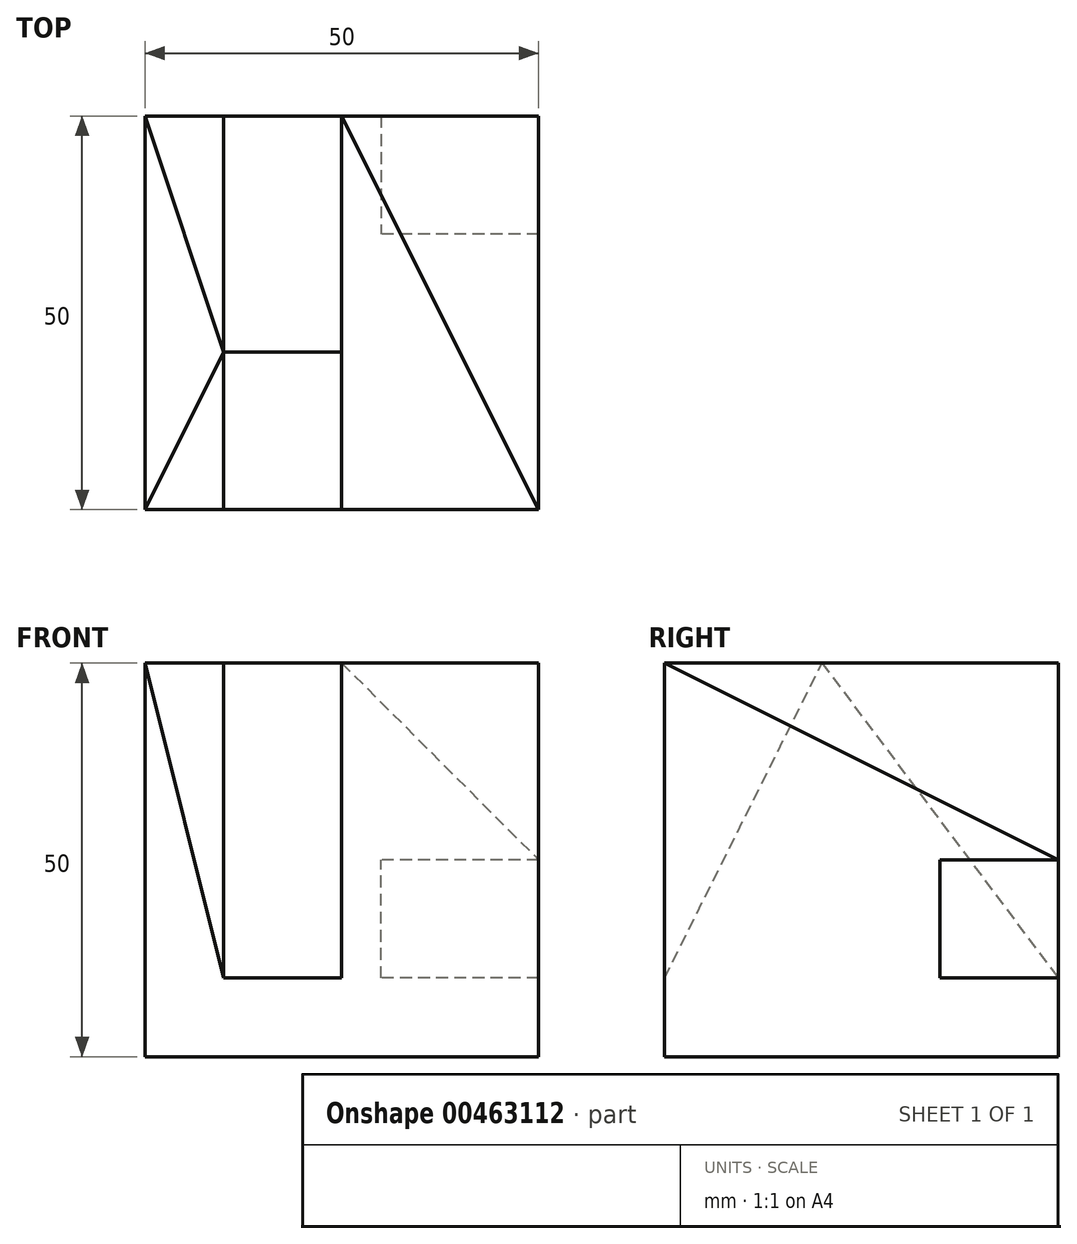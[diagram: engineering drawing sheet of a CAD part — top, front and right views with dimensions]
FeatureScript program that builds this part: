
annotation { "Feature Type Name" : "Feature", "Feature Type Description" : "" }
export const myFeature = defineFeature(function(context is Context, id is Id, definition is map)
    precondition{}
    {
        {
            var Q0;
            Q0=qCreatedBy(makeId("Top.planeOp"),FACE);
            var sketch = newSketch(context, id + "F0", { "sketchPlane" : qUnion([Q0])});
            skLineSegment(sketch, "E0.bottom", {"start": v(0, 0) * mm, "end": v(50, 0) * mm});
            skLineSegment(sketch, "E0.top", {"start": v(0, 50) * mm, "end": v(50, 50) * mm});
            skLineSegment(sketch, "E0.left", {"start": v(0, 0) * mm, "end": v(0, 50) * mm});
            skLineSegment(sketch, "E0.right", {"start": v(50, 0) * mm, "end": v(50, 50) * mm});
            skSolve(sketch);
        }
        {
            var Q0;
            Q0 = qSketchRegion(id + "F0", true);
            extrude(context, id + "F1", {"entities" : qUnion([Q0]), "depth" : 50 * mm});
        }
        {
            var Q0;
            Q0=makeQuery(id+"F1.opExtrude","CAP_FACE",FACE,{"disambiguationData":[OSD([sQuery(id+"F0.wireOp",EDGE,"E0.bottom"),sQuery(id+"F0.wireOp",EDGE,"E0.top"),sQuery(id+"F0.wireOp",EDGE,"E0.left"),sQuery(id+"F0.wireOp",EDGE,"E0.right")])],"isStart":false});
            var sketch = newSketch(context, id + "F2", { "sketchPlane" : qUnion([Q0])});
            skLineSegment(sketch, "E1", {"start": v(0, 50) * mm, "end": v(10, 50) * mm});
            skLineSegment(sketch, "E2", {"start": v(10, 50) * mm, "end": v(25, 50) * mm});
            skSolve(sketch);
        }
        {
            var Q0;
            Q0=makeQuery(id+"F2.imprint","IMPRINT",FACE,{"disambiguationData":[TD([[makeQuery(id+"F2.imprint","IMPRINT",EDGE,{"derivedFrom":sQuery(id+"F2.wireOp",EDGE,"E1")}),-1.0]])]});
            var sketch = newSketch(context, id + "F3", { "sketchPlane" : qUnion([Q0])});
            skLineSegment(sketch, "E3", {"start": v(0, 0) * mm, "end": v(0, 20) * mm});
            skLineSegment(sketch, "E4", {"start": v(0, 20) * mm, "end": v(50, 20) * mm});
            skLineSegment(sketch, "E5", {"start": v(0, 20) * mm, "end": v(10, 20) * mm});
            skLineSegment(sketch, "E6", {"start": v(10, 20) * mm, "end": v(25, 20) * mm});
            skSolve(sketch);
        }
        {
            var Q0;
            Q0=makeQuery(id+"F1.opExtrude","SWEPT_FACE",FACE,{"disambiguationData":[OSD([sQuery(id+"F0.wireOp",EDGE,"E0.bottom")])]});
            var sketch = newSketch(context, id + "F4", { "sketchPlane" : qUnion([Q0])});
            skLineSegment(sketch, "E7", {"start": v(0, 0) * mm, "end": v(10, 0) * mm});
            skLineSegment(sketch, "E8", {"start": v(10, 0) * mm, "end": v(25, 0) * mm});
            skLineSegment(sketch, "E9", {"start": v(0, 0) * mm, "end": v(0, 10) * mm});
            skLineSegment(sketch, "E10", {"start": v(10, 0) * mm, "end": v(10, 10) * mm});
            skLineSegment(sketch, "E11", {"start": v(25, 0) * mm, "end": v(25, 10) * mm});
            skSolve(sketch);
        }
        {
            var Q0;
            Q0=sQuery(id+"F3.wireOp",VERTEX,"E6.start");
            var Q1;
            Q1=sQuery(id+"F3.wireOp",VERTEX,"E6.end");
            var Q2;
            Q2=sQuery(id+"F4.wireOp",VERTEX,"E10.end");
            cPlane(context, id + "F5", {"entities" : qUnion([Q0, Q1, Q2]), "cplaneType" : CPlaneType.THREE_POINT, "offset" : 25 * mm, "width" : 150 * mm, "height" : 150 * mm});
        }
        {
            var Q0;
            Q0=qCreatedBy(id+"F5.planeOp",FACE);
            var sketch = newSketch(context, id + "F6", { "sketchPlane" : qUnion([Q0])});
            skLineSegment(sketch, "E12", {"start": v(10, 53.67) * mm, "end": v(10, 0) * mm});
            skLineSegment(sketch, "E13", {"start": v(10, 0) * mm, "end": v(25, 0) * mm});
            skLineSegment(sketch, "E14", {"start": v(25, 0) * mm, "end": v(25, 53.67) * mm});
            skLineSegment(sketch, "E15", {"start": v(25, 53.67) * mm, "end": v(10, 53.67) * mm});
            skSolve(sketch);
        }
        {
            var Q0;
            Q0 = qSketchRegion(id + "F6", true);
            extrude(context, id + "F7", {"entities" : qUnion([Q0]), "operationType" : NewBodyOperationType.REMOVE, "endBound" : BoundingType.UP_TO_NEXT, "depth" : 25 * mm});
        }
        {
            var Q0;
            Q0=makeQuery(id+"F1.opExtrude","SWEPT_FACE",FACE,{"disambiguationData":[OSD([sQuery(id+"F0.wireOp",EDGE,"E0.top")])]});
            var sketch = newSketch(context, id + "F8", { "sketchPlane" : qUnion([Q0])});
            skLineSegment(sketch, "E16", {"start": v(0, 0) * mm, "end": v(-10, 0) * mm});
            skLineSegment(sketch, "E17", {"start": v(-10, 0) * mm, "end": v(-25, 0) * mm});
            skLineSegment(sketch, "E18", {"start": v(-25, 0) * mm, "end": v(-25, 10) * mm});
            skLineSegment(sketch, "E19", {"start": v(-10, 0) * mm, "end": v(-10, 10) * mm});
            skSolve(sketch);
        }
        {
            var Q0;
            Q0=sQuery(id+"F3.wireOp",EDGE,"E4");
            cPoint(context, id + "F9", {"entities" : qUnion([Q0]), "parameter" : 0.5});
        }
        {
            var Q0;
            Q0 = qCreatedBy(id + "F9" ,VERTEX);
            var Q1;
            Q1=sQuery(id+"F3.wireOp",VERTEX,"E6.start");
            var Q2;
            Q2=sQuery(id+"F8.wireOp",VERTEX,"E18.end");
            cPlane(context, id + "F10", {"entities" : qUnion([Q0, Q1, Q2]), "cplaneType" : CPlaneType.THREE_POINT, "offset" : 25 * mm, "width" : 150 * mm, "height" : 150 * mm});
        }
        {
            var Q0;
            Q0=qCreatedBy(id+"F10.planeOp",FACE);
            var sketch = newSketch(context, id + "F11", { "sketchPlane" : qUnion([Q0])});
            skLineSegment(sketch, "E20", {"start": v(-10, 28) * mm, "end": v(-25, 28) * mm});
            skLineSegment(sketch, "E21", {"start": v(-25, 28) * mm, "end": v(-25, -30) * mm});
            skLineSegment(sketch, "E22", {"start": v(-25, -30) * mm, "end": v(-10, -30) * mm});
            skLineSegment(sketch, "E23", {"start": v(-10, -30) * mm, "end": v(-10, 28) * mm});
            skSolve(sketch);
        }
        {
            var Q0;
            Q0 = qSketchRegion(id + "F11", true);
            extrude(context, id + "F12", {"entities" : qUnion([Q0]), "operationType" : NewBodyOperationType.REMOVE, "endBound" : BoundingType.UP_TO_NEXT, "depth" : 25 * mm});
        }
        {
            var Q0;
            Q0=makeQuery(id+"F2.imprint","IMPRINT",FACE,{"disambiguationData":[TD([[makeQuery(id+"F2.imprint","IMPRINT",EDGE,{"derivedFrom":sQuery(id+"F2.wireOp",EDGE,"E1")}),-1.0]])]});
            var sketch = newSketch(context, id + "F13", { "sketchPlane" : qUnion([Q0])});
            skLineSegment(sketch, "E24", {"start": v(25, 50) * mm, "end": v(50, 0) * mm});
            skSolve(sketch);
        }
        {
            var Q0;
            Q0=makeQuery(id+"F1.opExtrude","SWEPT_FACE",FACE,{"disambiguationData":[OSD([sQuery(id+"F0.wireOp",EDGE,"E0.right")])]});
            var sketch = newSketch(context, id + "F14", { "sketchPlane" : qUnion([Q0])});
            skLineSegment(sketch, "E25", {"start": v(50, 50) * mm, "end": v(50, 25) * mm});
            skLineSegment(sketch, "E26", {"start": v(50, 0) * mm, "end": v(50, 10) * mm});
            skLineSegment(sketch, "E27", {"start": v(50, 25) * mm, "end": v(35, 25) * mm});
            skLineSegment(sketch, "E28", {"start": v(35, 25) * mm, "end": v(35, 10) * mm});
            skLineSegment(sketch, "E29", {"start": v(35, 10) * mm, "end": v(50, 10) * mm});
            skLineSegment(sketch, "E30", {"start": v(50, 25) * mm, "end": v(50, 10) * mm});
            skLineSegment(sketch, "E31", {"start": v(0, 50) * mm, "end": v(50, 25) * mm});
            skSolve(sketch);
        }
        {
            var Q0;
            Q0=sQuery(id+"F13.wireOp",VERTEX,"E24.end");
            var Q1;
            Q1=sQuery(id+"F2.wireOp",VERTEX,"E2.end");
            var Q2;
            Q2=sQuery(id+"F14.wireOp",VERTEX,"E30.start");
            cPlane(context, id + "F15", {"entities" : qUnion([Q0, Q1, Q2]), "cplaneType" : CPlaneType.THREE_POINT, "offset" : 25 * mm, "width" : 150 * mm, "height" : 150 * mm});
        }
        {
            var Q0;
            Q0=qCreatedBy(id+"F15.planeOp",FACE);
            var sketch = newSketch(context, id + "F16", { "sketchPlane" : qUnion([Q0])});
            skLineSegment(sketch, "E32", {"start": v(-23.57, 0) * mm, "end": v(29.46, 17.68) * mm});
            skLineSegment(sketch, "E33", {"start": v(29.46, 17.68) * mm, "end": v(29.46, -17.68) * mm});
            skLineSegment(sketch, "E34", {"start": v(29.46, -17.68) * mm, "end": v(-23.57, 0) * mm});
            skSolve(sketch);
        }
        {
            var Q0;
            Q0 = qSketchRegion(id + "F16", true);
            extrude(context, id + "F17", {"entities" : qUnion([Q0]), "operationType" : NewBodyOperationType.REMOVE, "endBound" : BoundingType.UP_TO_NEXT, "depth" : 25 * mm});
        }
        {
            var Q0;
            Q0=sQuery(id+"F3.wireOp",VERTEX,"E6.start");
            var Q1;
            Q1=sQuery(id+"F3.wireOp",VERTEX,"E3.start");
            var Q2;
            Q2=sQuery(id+"F4.wireOp",VERTEX,"E10.end");
            cPlane(context, id + "F18", {"entities" : qUnion([Q0, Q1, Q2]), "cplaneType" : CPlaneType.THREE_POINT, "offset" : 25 * mm, "width" : 150 * mm, "height" : 150 * mm});
        }
        {
            var Q0;
            Q0=qCreatedBy(id+"F18.planeOp",FACE);
            var sketch = newSketch(context, id + "F19", { "sketchPlane" : qUnion([Q0])});
            skLineSegment(sketch, "E35", {"start": v(-5.3, 48.5) * mm, "end": v(-27.52, 46.08) * mm});
            skLineSegment(sketch, "E36", {"start": v(-27.52, 46.08) * mm, "end": v(-5.3, 7.28) * mm});
            skLineSegment(sketch, "E37", {"start": v(-5.3, 7.28) * mm, "end": v(-5.3, 48.5) * mm});
            skSolve(sketch);
        }
        {
            var Q0;
            Q0 = qSketchRegion(id + "F19", true);
            extrude(context, id + "F20", {"entities" : qUnion([Q0]), "operationType" : NewBodyOperationType.REMOVE, "endBound" : BoundingType.UP_TO_NEXT, "oppositeDirection" : true, "depth" : 25 * mm});
        }
        {
            var Q0;
            Q0=sQuery(id+"F3.wireOp",VERTEX,"E6.start");
            var Q1;
            Q1=sQuery(id+"F2.wireOp",VERTEX,"E1.start");
            var Q2;
            Q2=sQuery(id+"F8.wireOp",VERTEX,"E19.end");
            cPlane(context, id + "F21", {"entities" : qUnion([Q0, Q1, Q2]), "cplaneType" : CPlaneType.THREE_POINT, "offset" : 25 * mm, "width" : 150 * mm, "height" : 150 * mm});
        }
        {
            var Q0;
            Q0=qCreatedBy(id+"F21.planeOp",FACE);
            var sketch = newSketch(context, id + "F22", { "sketchPlane" : qUnion([Q0])});
            skLineSegment(sketch, "E38", {"start": v(12.31, 46.08) * mm, "end": v(43.84, 7.28) * mm});
            skLineSegment(sketch, "E39", {"start": v(43.84, 7.28) * mm, "end": v(43.84, 48.5) * mm});
            skLineSegment(sketch, "E40", {"start": v(43.84, 48.5) * mm, "end": v(12.31, 46.08) * mm});
            skSolve(sketch);
        }
        {
            var Q0;
            Q0 = qSketchRegion(id + "F22", true);
            extrude(context, id + "F23", {"entities" : qUnion([Q0]), "operationType" : NewBodyOperationType.REMOVE, "endBound" : BoundingType.UP_TO_NEXT, "depth" : 25 * mm});
        }
        {
            var Q0;
            Q0=makeQuery(id+"F8.imprint","IMPRINT",FACE,{"disambiguationData":[TD([[makeQuery(id+"F8.imprint","IMPRINT",EDGE,{"derivedFrom":sQuery(id+"F8.wireOp",EDGE,"E16")}),-1.0]])]});
            var sketch = newSketch(context, id + "F24", { "sketchPlane" : qUnion([Q0])});
            skLineSegment(sketch, "E41", {"start": v(-50, 25) * mm, "end": v(-30, 25) * mm});
            skLineSegment(sketch, "E42", {"start": v(-50, 10) * mm, "end": v(-30, 10) * mm});
            skSolve(sketch);
        }
        {
            var Q0;
            Q0=makeQuery(id+"F4.imprint","IMPRINT",FACE,{"disambiguationData":[TD([[makeQuery(id+"F4.imprint","IMPRINT",EDGE,{"derivedFrom":sQuery(id+"F4.wireOp",EDGE,"E7")}),1.0]])]});
            var sketch = newSketch(context, id + "F25", { "sketchPlane" : qUnion([Q0])});
            skLineSegment(sketch, "E43", {"start": v(50, 0) * mm, "end": v(30, 0) * mm});
            skSolve(sketch);
        }
        {
            var Q0;
            Q0=sQuery(id+"F24.wireOp",VERTEX,"E41.end");
            var Q1;
            Q1=sQuery(id+"F24.wireOp",VERTEX,"E42.end");
            var Q2;
            Q2=sQuery(id+"F25.wireOp",VERTEX,"E43.end");
            cPlane(context, id + "F26", {"entities" : qUnion([Q0, Q1, Q2]), "cplaneType" : CPlaneType.THREE_POINT, "offset" : 25 * mm, "width" : 150 * mm, "height" : 150 * mm});
        }
        {
            var Q0;
            Q0=qCreatedBy(id+"F26.planeOp",FACE);
            var sketch = newSketch(context, id + "F27", { "sketchPlane" : qUnion([Q0])});
            skLineSegment(sketch, "E44", {"start": v(50, 25) * mm, "end": v(35, 25) * mm});
            skLineSegment(sketch, "E45", {"start": v(35, 25) * mm, "end": v(35, 10) * mm});
            skLineSegment(sketch, "E46", {"start": v(35, 10) * mm, "end": v(50, 10) * mm});
            skLineSegment(sketch, "E47", {"start": v(50, 10) * mm, "end": v(50, 25) * mm});
            skSolve(sketch);
        }
        {
            var Q0;
            Q0 = qSketchRegion(id + "F27", true);
            extrude(context, id + "F28", {"entities" : qUnion([Q0]), "operationType" : NewBodyOperationType.REMOVE, "endBound" : BoundingType.UP_TO_NEXT, "depth" : 25 * mm});
        }
    });
